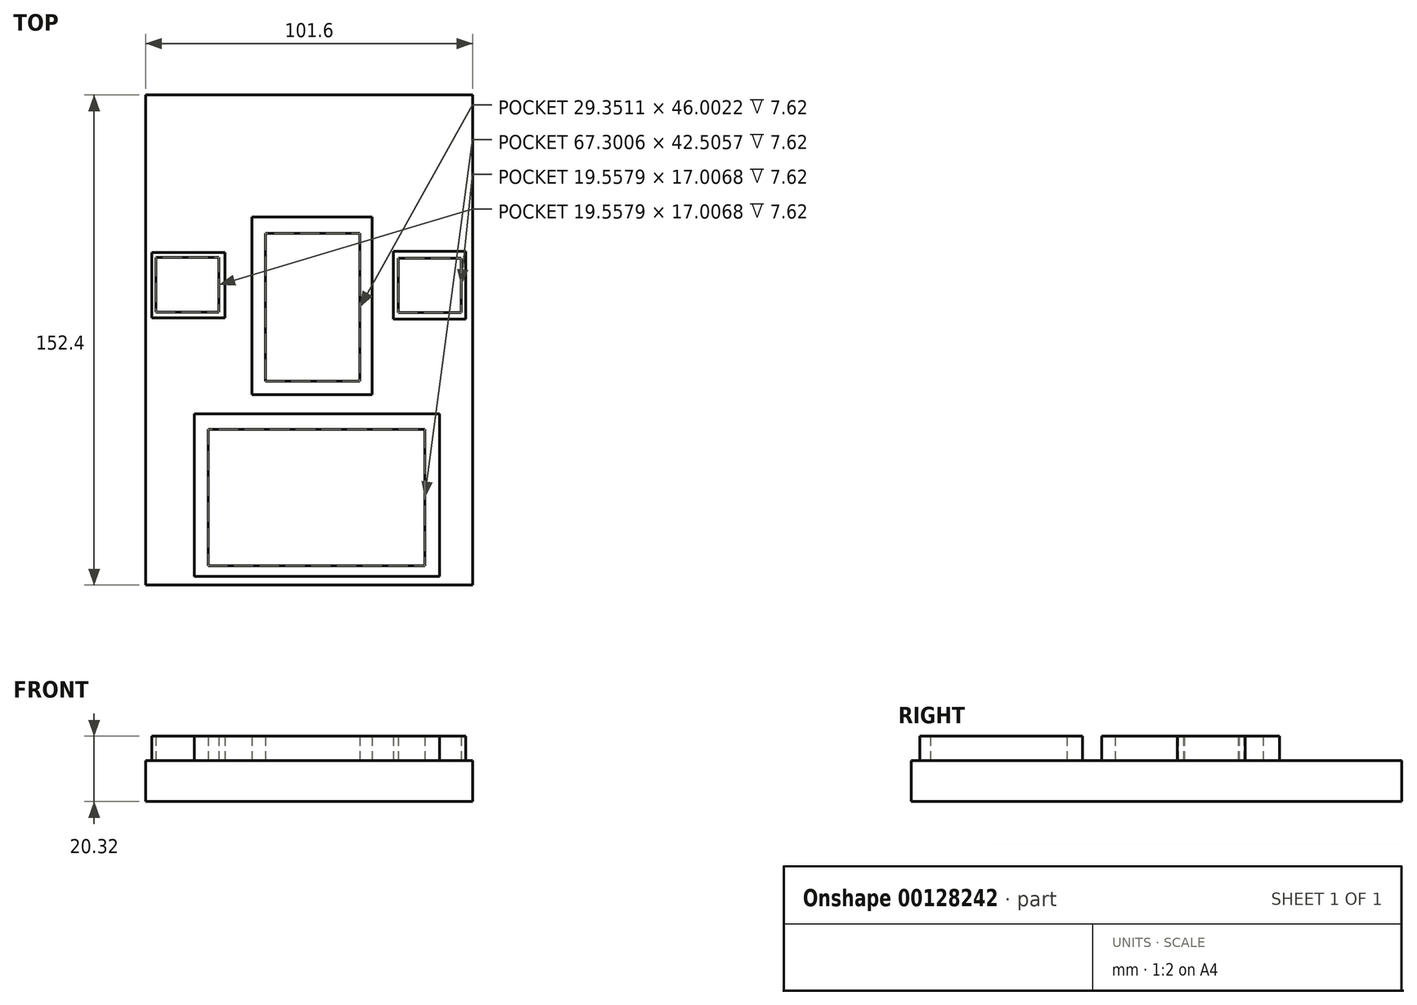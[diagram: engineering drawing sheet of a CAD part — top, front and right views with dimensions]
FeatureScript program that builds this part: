
annotation { "Feature Type Name" : "Feature", "Feature Type Description" : "" }
export const myFeature = defineFeature(function(context is Context, id is Id, definition is map)
    precondition{}
    {
        {
            var Q0;
            Q0=qCreatedBy(makeId("Top.planeOp"),FACE);
            var sketch = newSketch(context, id + "F0", { "sketchPlane" : qUnion([Q0])});
            skLineSegment(sketch, "E0.bottom", {"start": v(-51.36, 76.2) * mm, "end": v(50.24, 76.2) * mm});
            skLineSegment(sketch, "E0.top", {"start": v(-51.36, -76.2) * mm, "end": v(50.24, -76.2) * mm});
            skLineSegment(sketch, "E0.left", {"start": v(-51.36, 76.2) * mm, "end": v(-51.36, -76.2) * mm});
            skLineSegment(sketch, "E0.right", {"start": v(50.24, 76.2) * mm, "end": v(50.24, -76.2) * mm});
            skLineSegment(sketch, "E1.bottom", {"start": v(-12.67, 38.26) * mm, "end": v(13.29, 38.26) * mm});
            skLineSegment(sketch, "E1.top", {"start": v(-12.67, 0) * mm, "end": v(13.29, 0) * mm});
            skLineSegment(sketch, "E1.left", {"start": v(-12.67, 38.26) * mm, "end": v(-12.67, 0) * mm});
            skLineSegment(sketch, "E1.right", {"start": v(13.29, 38.26) * mm, "end": v(13.29, 0) * mm});
            skSolve(sketch);
        }
        {
            var Q0;
            Q0=makeQuery(id+"F0.imprint","IMPRINT",FACE,{"disambiguationData":[TD([[makeQuery(id+"F0.imprint","IMPRINT",EDGE,{"derivedFrom":sQuery(id+"F0.wireOp",EDGE,"E1.bottom")}),-1.0]])]});
            var Q1;
            Q1=makeQuery(id+"F0.imprint","IMPRINT",FACE,{"disambiguationData":[TD([[makeQuery(id+"F0.imprint","IMPRINT",EDGE,{"derivedFrom":sQuery(id+"F0.wireOp",EDGE,"E0.bottom")}),-1.0]])]});
            extrude(context, id + "F1", {"entities" : qUnion([Q0, Q1]), "depth" : 12.7 * mm});
        }
        {
            var Q0;
            Q0=makeQuery(id+"F1.opExtrude","CAP_FACE",FACE,{"disambiguationData":[OSD([sQuery(id+"F0.wireOp",EDGE,"E0.bottom"),sQuery(id+"F0.wireOp",EDGE,"E0.top"),sQuery(id+"F0.wireOp",EDGE,"E0.left"),sQuery(id+"F0.wireOp",EDGE,"E0.right")])],"isStart":false});
            var sketch = newSketch(context, id + "F2", { "sketchPlane" : qUnion([Q0])});
            skLineSegment(sketch, "E2.bottom", {"start": v(-14.11, 33.16) * mm, "end": v(15.24, 33.16) * mm});
            skLineSegment(sketch, "E2.top", {"start": v(-14.11, -12.84) * mm, "end": v(15.24, -12.84) * mm});
            skLineSegment(sketch, "E2.left", {"start": v(-14.11, 33.16) * mm, "end": v(-14.11, -12.84) * mm});
            skLineSegment(sketch, "E2.right", {"start": v(15.24, 33.16) * mm, "end": v(15.24, -12.84) * mm});
            skLineSegment(sketch, "E3.bottom", {"start": v(18.97, -17.03) * mm, "end": v(-18.38, -17.03) * mm});
            skLineSegment(sketch, "E3.top", {"start": v(18.97, 38.29) * mm, "end": v(-18.38, 38.29) * mm});
            skLineSegment(sketch, "E3.left", {"start": v(18.97, -17.03) * mm, "end": v(18.97, 38.29) * mm});
            skLineSegment(sketch, "E3.right", {"start": v(-18.38, -17.03) * mm, "end": v(-18.38, 38.29) * mm});
            skLineSegment(sketch, "E4.bottom", {"start": v(-31.9, -27.72) * mm, "end": v(35.4, -27.72) * mm});
            skLineSegment(sketch, "E4.top", {"start": v(-31.9, -70.23) * mm, "end": v(35.4, -70.23) * mm});
            skLineSegment(sketch, "E4.left", {"start": v(-31.9, -27.72) * mm, "end": v(-31.9, -70.23) * mm});
            skLineSegment(sketch, "E4.right", {"start": v(35.4, -27.72) * mm, "end": v(35.4, -70.23) * mm});
            skLineSegment(sketch, "E5.bottom", {"start": v(-36.26, -22.93) * mm, "end": v(39.96, -22.93) * mm});
            skLineSegment(sketch, "E5.top", {"start": v(-36.26, -73.52) * mm, "end": v(39.96, -73.52) * mm});
            skLineSegment(sketch, "E5.left", {"start": v(-36.26, -22.93) * mm, "end": v(-36.26, -73.52) * mm});
            skLineSegment(sketch, "E5.right", {"start": v(39.96, -22.93) * mm, "end": v(39.96, -73.52) * mm});
            skLineSegment(sketch, "E6.bottom", {"start": v(27.1, 25.5) * mm, "end": v(46.67, 25.5) * mm});
            skLineSegment(sketch, "E6.top", {"start": v(27.1, 8.5) * mm, "end": v(46.67, 8.5) * mm});
            skLineSegment(sketch, "E6.left", {"start": v(27.1, 25.5) * mm, "end": v(27.1, 8.5) * mm});
            skLineSegment(sketch, "E6.right", {"start": v(46.67, 25.5) * mm, "end": v(46.67, 8.5) * mm});
            skLineSegment(sketch, "E7.bottom", {"start": v(25.66, 27.63) * mm, "end": v(48.08, 27.63) * mm});
            skLineSegment(sketch, "E7.top", {"start": v(25.66, 6.56) * mm, "end": v(48.08, 6.56) * mm});
            skLineSegment(sketch, "E7.left", {"start": v(25.66, 27.63) * mm, "end": v(25.66, 6.56) * mm});
            skLineSegment(sketch, "E7.right", {"start": v(48.08, 27.63) * mm, "end": v(48.08, 6.56) * mm});
            skLineSegment(sketch, "E8.bottom", {"start": v(-48.16, 25.68) * mm, "end": v(-28.6, 25.68) * mm});
            skLineSegment(sketch, "E8.top", {"start": v(-48.16, 8.68) * mm, "end": v(-28.6, 8.68) * mm});
            skLineSegment(sketch, "E8.left", {"start": v(-48.16, 25.68) * mm, "end": v(-48.16, 8.68) * mm});
            skLineSegment(sketch, "E8.right", {"start": v(-28.6, 25.68) * mm, "end": v(-28.6, 8.68) * mm});
            skLineSegment(sketch, "E9.bottom", {"start": v(-49.47, 27.25) * mm, "end": v(-26.66, 27.25) * mm});
            skLineSegment(sketch, "E9.top", {"start": v(-49.47, 6.84) * mm, "end": v(-26.66, 6.84) * mm});
            skLineSegment(sketch, "E9.left", {"start": v(-49.47, 27.25) * mm, "end": v(-49.47, 6.84) * mm});
            skLineSegment(sketch, "E9.right", {"start": v(-26.66, 27.25) * mm, "end": v(-26.66, 6.84) * mm});
            skSolve(sketch);
        }
        {
            var Q0;
            Q0 = qSketchRegion(id + "F2", true);
            extrude(context, id + "F3", {"entities" : qUnion([Q0]), "operationType" : NewBodyOperationType.ADD, "depth" : 7.62 * mm});
        }
    });
